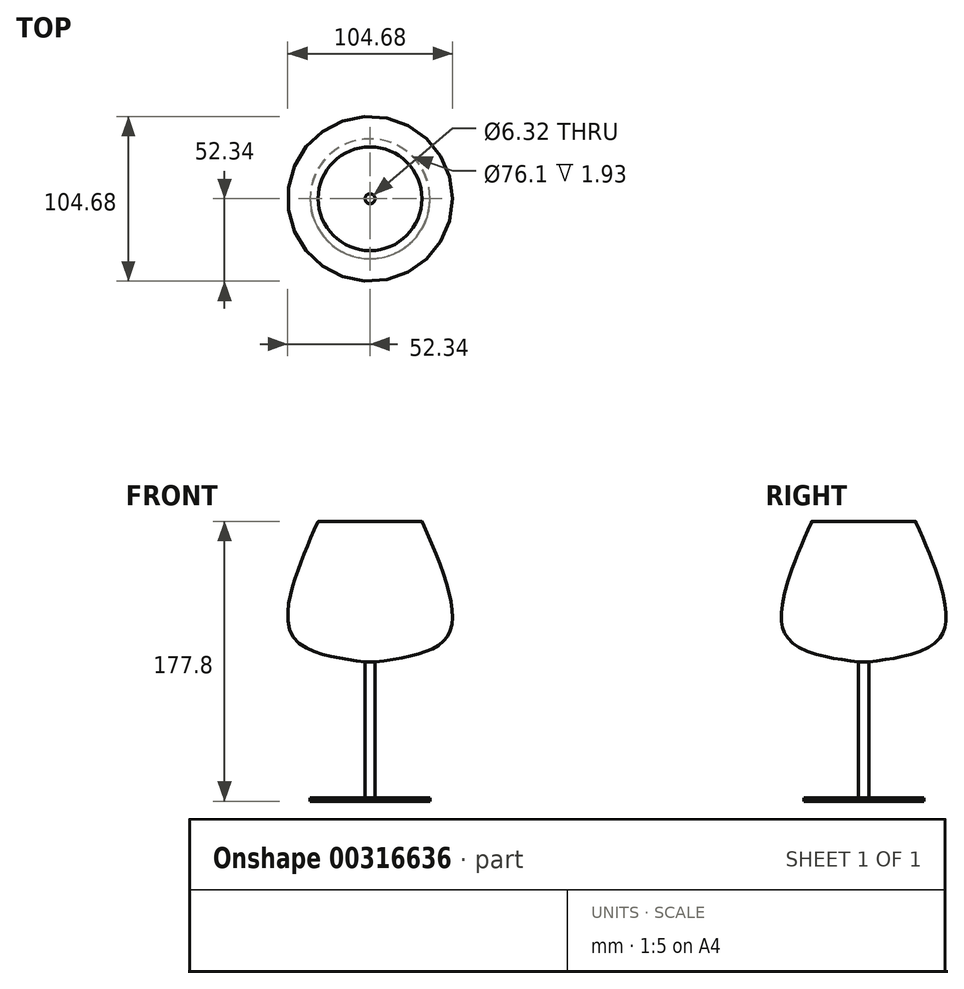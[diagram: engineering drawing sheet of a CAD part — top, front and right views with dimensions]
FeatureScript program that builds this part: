
annotation { "Feature Type Name" : "Feature", "Feature Type Description" : "" }
export const myFeature = defineFeature(function(context is Context, id is Id, definition is map)
    precondition{}
    {
        {
            var Q0;
            Q0=qCreatedBy(makeId("Front.planeOp"),FACE);
            var sketch = newSketch(context, id + "F0", { "sketchPlane" : qUnion([Q0])});
            skLineSegment(sketch, "E0", {"start": v(0, 0) * mm, "end": v(0, 177.8) * mm, "construction": true});
            skLineSegment(sketch, "E1", {"start": v(0, 0) * mm, "end": v(-38.1, 0) * mm});
            skLineSegment(sketch, "E2", {"start": v(-38.1, 0) * mm, "end": v(-38.1, 2.03) * mm});
            skLineSegment(sketch, "E3", {"start": v(-38.1, 2.03) * mm, "end": v(0, 2.03) * mm});
            skLineSegment(sketch, "E4", {"start": v(-3.21, 2.03) * mm, "end": v(-3.21, 88.4) * mm});
            skLineSegment(sketch, "E5", {"start": v(0, 177.8) * mm, "end": v(-33.02, 177.8) * mm});
            skFitSpline(sketch, "E6", {"points": [v(-3.21, 88.4) * mm, v(-49.88, 106.1) * mm, v(-33.02, 177.8) * mm], "startDerivative": vector(-133.64, 18.56) * mm, "endDerivative": vector(67.53, 155.82) * mm});
            skLineSegment(sketch, "E7", {"start": v(0, 177.8) * mm, "end": v(0, 0) * mm});
            skSolve(sketch);
        }
        {
            var Q0;
            {var subQ5=sQuery(id+"F0.wireOp",EDGE,"E1");Q0=makeQuery(id+"F0.imprint","IMPRINT",FACE,{"disambiguationData":[TD([[makeQuery(id+"F0.imprint","IMPRINT",EDGE,{"derivedFrom":subQ5}),-1.0]])]});}
            var Q1;
            {var subQ1=sQuery(id+"F0.wireOp",EDGE,"E4");Q1=makeQuery(id+"F0.imprint","IMPRINT",FACE,{"disambiguationData":[TD([[makeQuery(id+"F0.imprint","IMPRINT",EDGE,{"derivedFrom":subQ1}),-1.0]])]});}
            var Q2;
            Q2=sQuery(id+"F0.wireOp",EDGE,"E7");
            revolve(context, id + "F1", {"entities" : qUnion([Q0, Q1]), "axis" : qUnion([Q2]), "revolveType" : RevolveType.FULL});
        }
        {
            var Q0;
            Q0=makeQuery(id+"F1.opRevolve","SWEPT_FACE",FACE,{"disambiguationData":[OSD([sQuery(id+"F0.wireOp",EDGE,"E5")])]});
            shell(context, id + "F2", {"entities" : qUnion([Q0]), "thickness" : 0.05 * mm});
        }
        {
            var Q0;
            Q0=makeQuery(id+"F1.opRevolve","SWEPT_EDGE",EDGE,{"disambiguationData":[OSD([sQuery(id+"F0.wireOp",EDGE,"E5"),sQuery(id+"F0.wireOp",EDGE,"E6")])]});
            fillet(context, id + "F3", {"entities" : qUnion([Q0]), "radius" : 5.08 * mm, "tangentPropagation" : true, "allowEdgeOverflow" : false});
        }
    });
